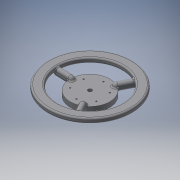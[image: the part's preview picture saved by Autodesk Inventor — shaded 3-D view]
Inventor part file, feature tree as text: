
AUTODESK INVENTOR PART (.ipt)
format: ipt  version: 2017 (Build 210142000, 142)  size: 749,568 bytes
history: native  units: mm
features: reference x6, extrude x3, sketch x3, fillet x2, chamfer x2, other x2, plane x1, pattern_circular x1
ambient origin geometry x8: Origin, YZ Plane, XZ Plane, XY Plane, X Axis, Y Axis, Z Axis, Center Point
bodies: Solid1 (feature_tree)
feature tree (20):
  extrude  "Extrusion1"  Depth=20.0mm
  plane  "Work Plane1"
  extrude  "Extrusion2"  Depth=80.0mm
  extrude  "Extrusion3"  Depth=10.0mm TaperAngle=0.0deg
  pattern_circular  "Circular Pattern1"  [2 undecoded]
  fillet  "Fillet1"  Radius=170.0mm
  fillet  "Fillet2"  Radius=20.0mm
  chamfer  "Chamfer1"  Distance=10.0mm
  chamfer  "Chamfer2"  Distance=10.0mm
  sketch  "Sketch1"  dims[d0=8.0mm d1=20.0mm]
  sketch  "Sketch2"  dims[d2=20.0mm d3=80.0mm]
  sketch  "Sketch3"  dims[d4=4.5mm d5=10.0mm d6=0.0mm d7=1.0mm d8=170.0mm d9=20.0mm d10=10.0mm d11=0.0mm d12=10.0mm d13=0.0mm d14=30.0mm d15=360.0deg d17=5.0mm d18=3.0mm d19=15.0mm d20=2.0mm d21=2.0mm d22=45.0deg d23=2.0mm d24=2.0mm d25=45.0deg]
  reference  "Reference1"
  reference  "Reference2"
  reference  "Reference3"
  reference  "Reference4"
  reference  "Reference5"
  reference  "Reference6"
  other  "peristaltic pump.iam"
  other  "rotor 1:1"
note: 2 required parameter values undecoded (feature->parameter linkage not recoverable at this tier; creation-order binding heuristic only, values carry confidence <= 0.55)
